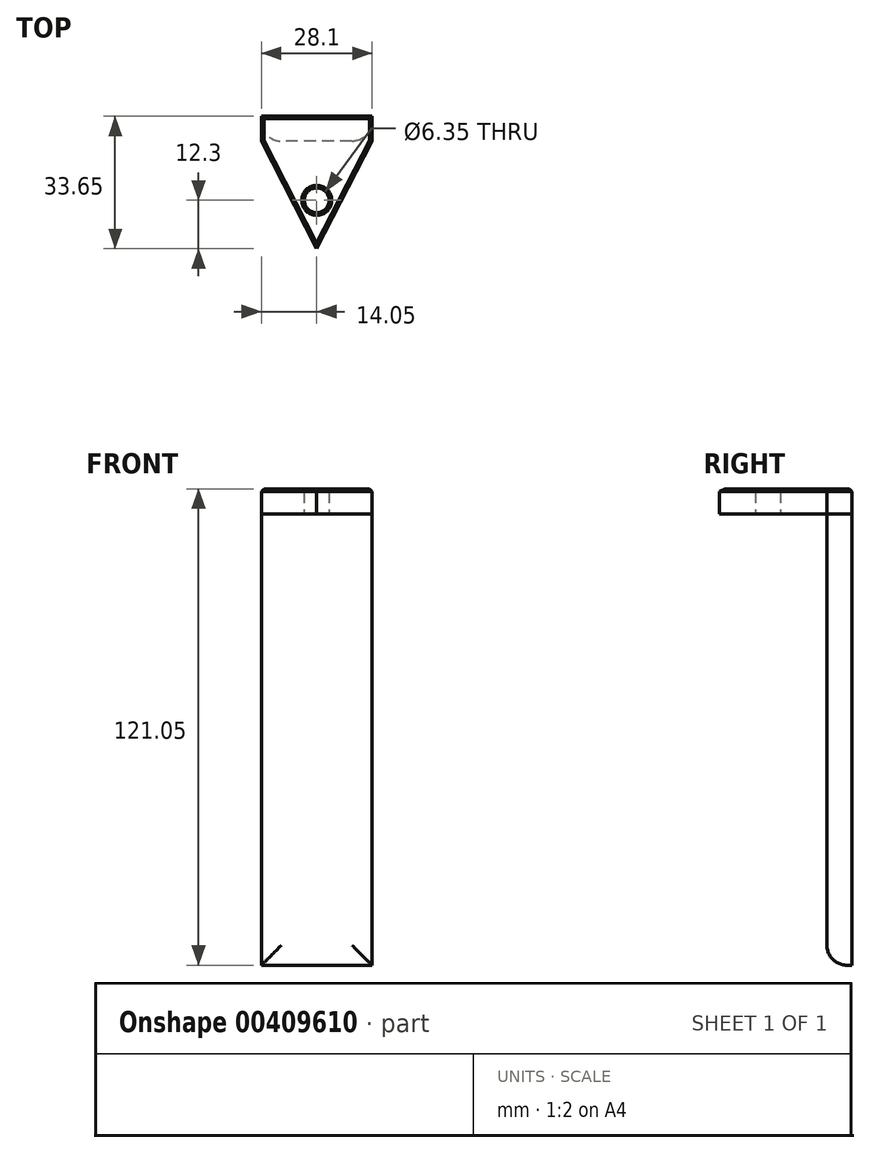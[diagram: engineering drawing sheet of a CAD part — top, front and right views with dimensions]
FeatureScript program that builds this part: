
annotation { "Feature Type Name" : "Feature", "Feature Type Description" : "" }
export const myFeature = defineFeature(function(context is Context, id is Id, definition is map)
    precondition{}
    {
        {
            var Q0;
            Q0=qCreatedBy(makeId("Front.planeOp"),FACE);
            var sketch = newSketch(context, id + "F0", { "sketchPlane" : qUnion([Q0])});
            skLineSegment(sketch, "E0.bottom", {"start": v(14.05, -57.35) * mm, "end": v(-14.05, -57.35) * mm});
            skLineSegment(sketch, "E0.top", {"start": v(14.05, 57.35) * mm, "end": v(-14.05, 57.35) * mm});
            skLineSegment(sketch, "E0.left", {"start": v(14.05, -57.35) * mm, "end": v(14.05, 57.35) * mm});
            skLineSegment(sketch, "E0.right", {"start": v(-14.05, -57.35) * mm, "end": v(-14.05, 57.35) * mm});
            skPoint(sketch, "E0.middle", {"position": v(0, 0) * mm});
            skSolve(sketch);
        }
        {
            var Q0;
            Q0=makeQuery(id+"F0.imprint","IMPRINT",FACE,{"disambiguationData":[TD([[makeQuery(id+"F0.imprint","IMPRINT",EDGE,{"derivedFrom":sQuery(id+"F0.wireOp",EDGE,"E0.bottom")}),-1.0]])]});
            extrude(context, id + "F1", {"entities" : qUnion([Q0]), "endBound" : BoundingType.SYMMETRIC, "depth" : 6.35 * mm});
        }
        {
            var Q0;
            Q0=makeQuery(id+"F1.opExtrude","SWEPT_FACE",FACE,{"disambiguationData":[OSD([sQuery(id+"F0.wireOp",EDGE,"E0.top")])]});
            var sketch = newSketch(context, id + "F2", { "sketchPlane" : qUnion([Q0])});
            skLineSegment(sketch, "E1", {"start": v(-14.05, -3.18) * mm, "end": v(0, -30.48) * mm});
            skLineSegment(sketch, "E2", {"start": v(14.05, -3.18) * mm, "end": v(0, -30.48) * mm});
            skPoint(sketch, "E3", {"position": v(0, -18.18) * mm});
            skLineSegment(sketch, "E4", {"start": v(-14.05, -3.18) * mm, "end": v(-14.05, 3.18) * mm});
            skLineSegment(sketch, "E5", {"start": v(-14.05, 3.18) * mm, "end": v(14.05, 3.18) * mm});
            skLineSegment(sketch, "E6", {"start": v(14.05, 3.18) * mm, "end": v(14.05, -3.18) * mm});
            skPoint(sketch, "E7", {"position": v(0, -23.1) * mm});
            skPoint(sketch, "E8", {"position": v(0, -11.68) * mm});
            skSolve(sketch);
        }
        {
            var Q0;
            Q0 = qSketchRegion(id + "F2", true);
            extrude(context, id + "F3", {"entities" : qUnion([Q0]), "depth" : 6.35 * mm});
        }
        {
            var Q0;
            Q0=sQuery(id+"F2.wireOp",VERTEX,"E3");
            var Q1;
            Q1=makeQuery(id+"F3.opExtrude","SWEPT_BODY",BODY,{"disambiguationData":[OSD([sQuery(id+"F2.wireOp",EDGE,"E1"),sQuery(id+"F2.wireOp",EDGE,"E2"),sQuery(id+"F2.wireOp",EDGE,"E4"),sQuery(id+"F2.wireOp",EDGE,"E5"),sQuery(id+"F2.wireOp",EDGE,"E6")])]});
            hole(context, id + "F4", {"style" : HoleStyle.SIMPLE, "endStyle" : HoleEndStyle.THROUGH, "oppositeDirection" : true, "holeDiameter" : 6.35 * mm, "isTappedThrough" : true, "tappedDepth" : 12.7 * mm, "tapClearance" : 3, "locations" : qUnion([Q0]), "scope" : qUnion([Q1])});
        }
        {
            var Q0;
            Q0=makeQuery(id+"F3.opExtrude","CAP_FACE",FACE,{"disambiguationData":[OSD([sQuery(id+"F2.wireOp",EDGE,"E1"),sQuery(id+"F2.wireOp",EDGE,"E2"),sQuery(id+"F2.wireOp",EDGE,"E4"),sQuery(id+"F2.wireOp",EDGE,"E5"),sQuery(id+"F2.wireOp",EDGE,"E6")])],"isStart":false});
            chamfer(context, id + "F5", {"entities" : qUnion([Q0]), "width" : 0.64 * mm, "tangentPropagation" : true});
        }
        {
            var Q0;
            Q0=makeQuery(id+"F1.opExtrude","CAP_EDGE",EDGE,{"disambiguationData":[OSD([sQuery(id+"F0.wireOp",EDGE,"E0.right")])],"isStart":false});
            var Q1;
            Q1=makeQuery(id+"F1.opExtrude","CAP_EDGE",EDGE,{"disambiguationData":[OSD([sQuery(id+"F0.wireOp",EDGE,"E0.bottom")])],"isStart":false});
            var Q2;
            Q2=makeQuery(id+"F1.opExtrude","CAP_EDGE",EDGE,{"disambiguationData":[OSD([sQuery(id+"F0.wireOp",EDGE,"E0.left")])],"isStart":false});
            fillet(context, id + "F6", {"entities" : qUnion([Q0, Q1, Q2]), "radius" : 5.08 * mm, "tangentPropagation" : true, "allowEdgeOverflow" : false});
        }
    });
